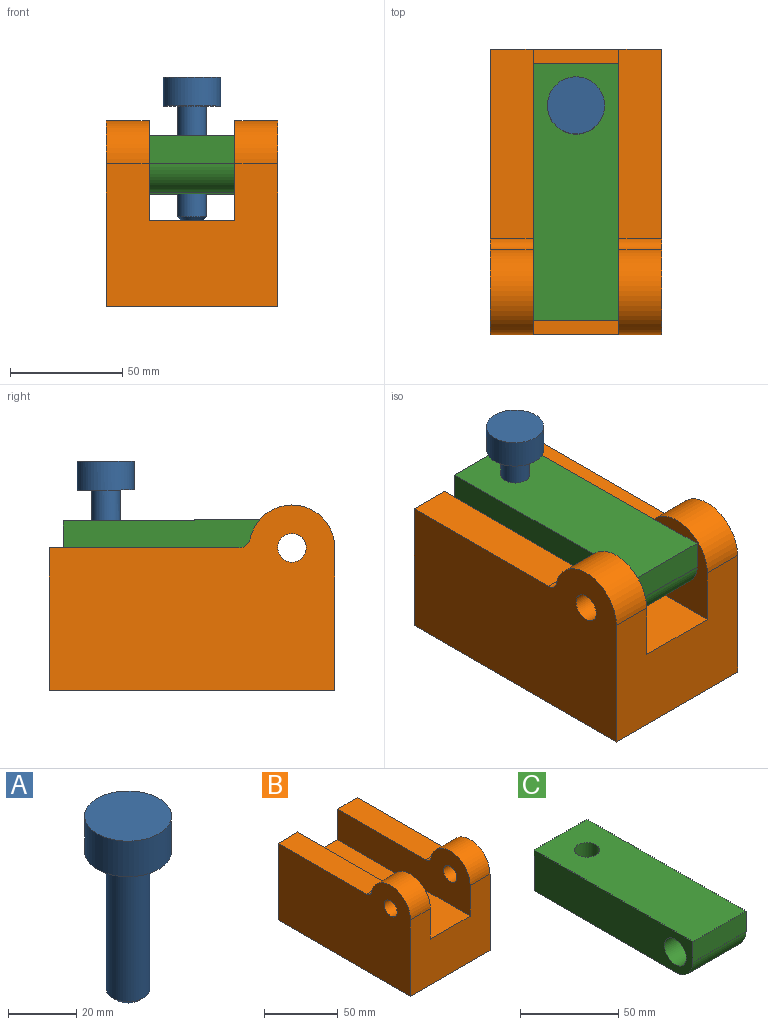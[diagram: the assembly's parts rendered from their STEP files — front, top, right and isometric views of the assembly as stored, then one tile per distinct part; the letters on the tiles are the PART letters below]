
ASSEMBLY  parts=3 mates=4
PART A: 6 faces, bbox 25.4x25.4x63.5 mm
  f0: cylinder r=6.35mm len=49.21mm, axis (0,0,-1), area 1963.5mm2, adj f4,f5
  f1: plane 9.53x9.53mm, normal (0,0,-1), area 71.3mm2, adj f5
  f2: cylinder r=12.7mm len=25.4mm, axis (0,0,-1), area 1013.4mm2, adj f3,f4
  f3: plane 25.4x25.4mm, normal (0,0,1), area 506.7mm2, adj f2
  f4: plane 25.4x25.4mm, normal (0,0,-1), area 380mm2, adj f0,f2
  f5: cone r=6.35mm half-angle=45deg, axis (0,0,1), area 78.4mm2, adj f0,f1
PART B: 16 faces, bbox 76.2x127x82.6 mm
  f0: plane 84.36x19.05mm, normal (0,0,1), area 1607.1mm2, adj f4,f5,f7,f15
  f1: plane 127x38.1mm, normal (0,0,1), area 4838.7mm2, adj f3,f5,f7,f8
  f2: plane 127x82.55mm, normal (-1,0,0), area 8511.8mm2, adj f3,f5,f6,f9,f11,f12,f14
  f3: plane 76.2x63.5mm, normal (0,-1,0), area 3871mm2, adj f1,f2,f4,f6,f7,f8,f10,f11
  f4: plane 127x82.55mm, normal (1,0,0), area 8511.8mm2, adj f0,f3,f5,f6,f10,f13,f15
  f5: plane 76.2x63.5mm, normal (0,1,0), area 3871mm2, adj f0,f1,f2,f4,f6,f7,f8,f9
  f6: plane 127x76.2mm, normal (0,0,-1), area 9677.4mm2, adj f2,f3,f4,f5
  f7: plane 127x44.45mm, normal (-1,0,0), area 3673.1mm2, adj f0,f1,f3,f5,f10,f13,f15
  f8: plane 127x44.45mm, normal (1,0,0), area 3673.1mm2, adj f1,f3,f5,f9,f11,f12,f14
  f9: plane 84.36x19.05mm, normal (0,0,1), area 1607.1mm2, adj f2,f5,f8,f14
  f10: cylinder r=19.05mm len=37.67mm, axis (1,0,0), area 1063.1mm2, adj f3,f4,f7,f15
  f11: cylinder r=19.05mm len=37.67mm, axis (-1,0,0), area 1063.1mm2, adj f2,f3,f8,f14
  f12: cylinder r=6.35mm len=19.05mm, axis (1,0,0), area 760.1mm2, adj f2,f8
  f13: cylinder r=6.35mm len=19.05mm, axis (1,0,0), area 760.1mm2, adj f4,f7
  f14: cylinder r=5.08mm len=19.05mm, axis (-1,0,0), area 131.5mm2, adj f2,f8,f9,f11
  f15: cylinder r=5.08mm len=19.05mm, axis (1,0,0), area 131.5mm2, adj f0,f4,f7,f10
PART C: 9 faces, bbox 38.1x114.3x25.4 mm
  f0: plane 114.3x25.4mm, normal (-1,0,0), area 2671mm2, adj f1,f3,f4,f5,f6,f7
  f1: plane 38.1x12.7mm, normal (0,-1,0), area 483.9mm2, adj f0,f2,f4,f6
  f2: plane 114.3x25.4mm, normal (1,0,0), area 2671mm2, adj f1,f3,f4,f5,f6,f7
  f3: plane 38.1x25.4mm, normal (0,1,0), area 967.7mm2, adj f0,f2,f4,f5
  f4: plane 114.3x38.1mm, normal (0,0,1), area 4228.2mm2, adj f0,f1,f2,f3,f8
  f5: plane 101.6x38.1mm, normal (0,0,-1), area 3744.3mm2, adj f0,f2,f3,f6,f8
  f6: cylinder r=12.7mm len=38.1mm, axis (1,0,0), area 760.1mm2, adj f0,f1,f2,f5
  f7: cylinder r=7.93mm len=38.1mm, axis (1,0,0), area 1898.6mm2, adj f0,f2
  f8: cylinder r=6.35mm len=25.4mm, axis (0,0,1), area 1013.4mm2, adj f4,f5
PLACE A rot(axis=(0,0,1),156.2deg) t=(105.88,117,120.24)mm
PLACE B t=(67.78,15.58,81.88)mm fixed
PLACE C rot(axis=(-1,0,0),0.4deg) t=(86.83,21.84,132.78)mm
MATE planar C.f2 <-> B.f7  axis (1,0,0) through (124.93,83.08,145.14)mm
MATE cylindrical C.f6 <-> B.f10  axis (1,0,0) through (124.93,34.63,145.38)mm
MATE cylindrical A.f0 <-> C.f8  axis (0,-0.01,-1) through (105.88,117.19,146.44)mm
MATE parallel B.f7 <-> C.f2  axis (-1,0,0) through (124.93,73.69,135.48)mm
